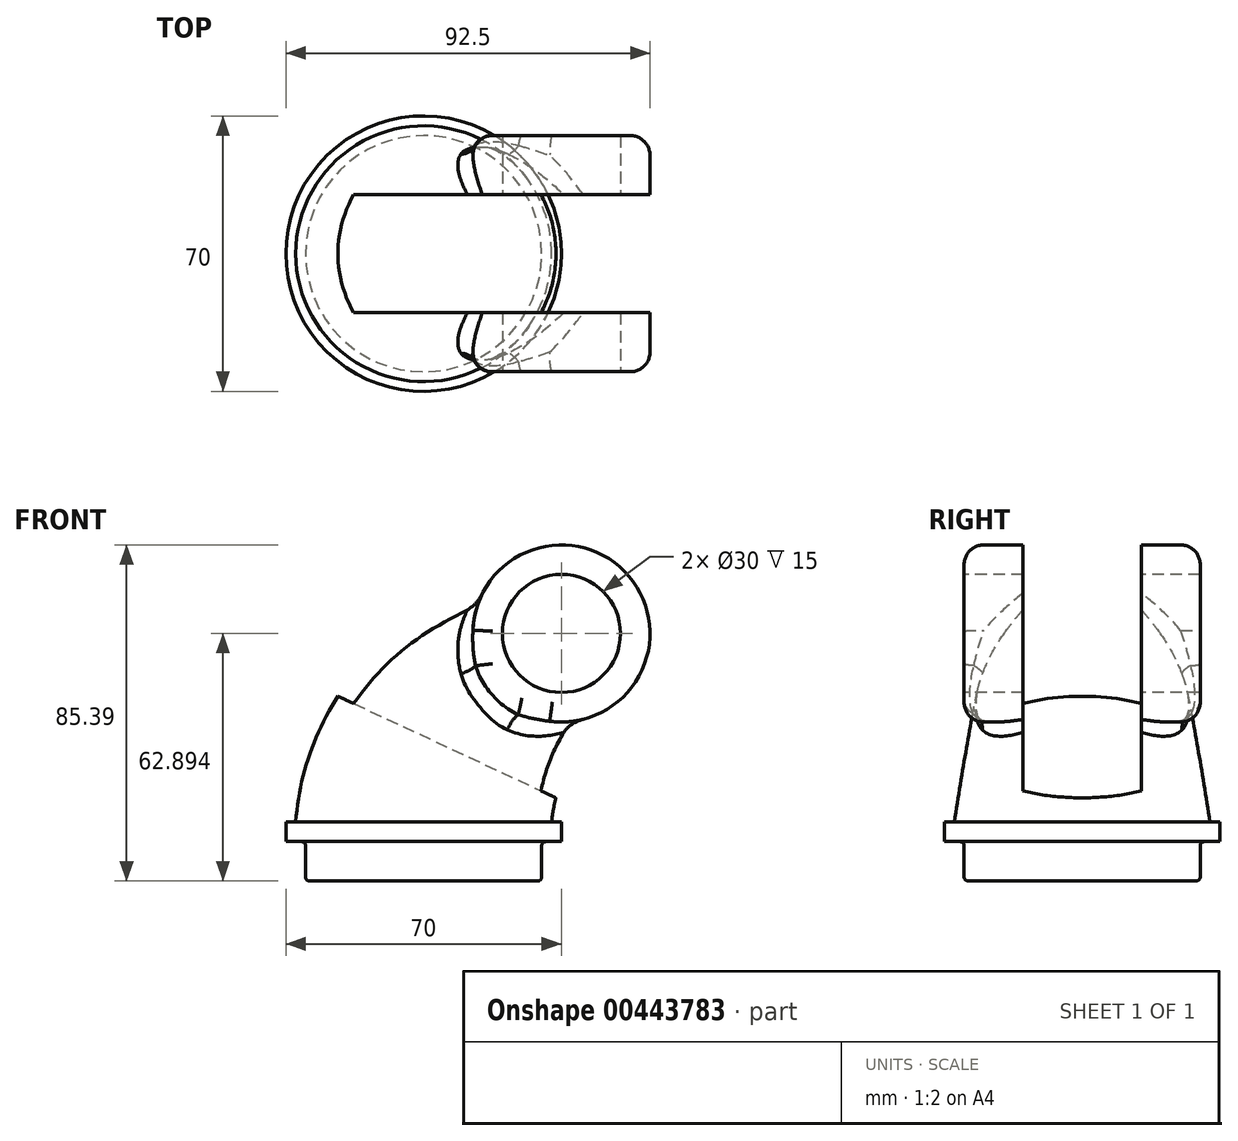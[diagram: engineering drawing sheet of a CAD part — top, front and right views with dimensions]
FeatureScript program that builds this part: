
annotation { "Feature Type Name" : "Feature", "Feature Type Description" : "" }
export const myFeature = defineFeature(function(context is Context, id is Id, definition is map)
    precondition{}
    {
        {
            var Q0;
            Q0=qCreatedBy(makeId("Top.planeOp"),FACE);
            var sketch = newSketch(context, id + "F0", { "sketchPlane" : qUnion([Q0])});
            skCircle(sketch, "E0", {"center": v(0, 0) * mm, "radius": 35 * mm});
            skSolve(sketch);
        }
        {
            var Q0;
            Q0 = qSketchRegion(id + "F0", true);
            extrude(context, id + "F1", {"entities" : qUnion([Q0]), "depth" : 5 * mm});
        }
        {
            var Q0;
            Q0=qCreatedBy(makeId("Front.planeOp"),FACE);
            var sketch = newSketch(context, id + "F2", { "sketchPlane" : qUnion([Q0])});
            skArc(sketch, "E1", {"start": v(17.6, 38.3) * mm, "mid": v(5.55, 23.37) * mm, "end": v(0, 5) * mm});
            skLineSegment(sketch, "E2", {"start": v(17.6, 38.3) * mm, "end": v(35, 52.9) * mm});
            skSolve(sketch);
        }
        {
            var Q0;
            Q0=sQuery(id+"F2.wireOp",EDGE,"E2");
            var Q1;
            Q1=sQuery(id+"F2.wireOp",VERTEX,"E2.end");
            cPlane(context, id + "F3", {"entities" : qUnion([Q0, Q1]), "cplaneType" : CPlaneType.LINE_POINT, "offset" : 25 * mm, "width" : 150 * mm, "height" : 150 * mm});
        }
        {
            var Q0;
            Q0=qCreatedBy(id+"F3.planeOp",FACE);
            var sketch = newSketch(context, id + "F4", { "sketchPlane" : qUnion([Q0])});
            skCircle(sketch, "E3", {"center": v(0, 18.02) * mm, "radius": 22.5 * mm});
            skSolve(sketch);
        }
        {
            var Q0;
            Q0=makeQuery(id+"F1.opExtrude","CAP_FACE",FACE,{"disambiguationData":[OSD([sQuery(id+"F0.wireOp",EDGE,"E0")])],"isStart":false});
            var sketch = newSketch(context, id + "F5", { "sketchPlane" : qUnion([Q0])});
            skCircle(sketch, "E4", {"center": v(0, 0) * mm, "radius": 32.5 * mm});
            skSolve(sketch);
        }
        {
            var Q0;
            Q0=qCreatedBy(makeId("Front.planeOp"),FACE);
            var sketch = newSketch(context, id + "F6", { "sketchPlane" : qUnion([Q0])});
            skArc(sketch, "E5", {"start": v(0.95, 58.66) * mm, "mid": v(-22.4, 35.96) * mm, "end": v(-32.5, 5) * mm});
            skLineSegment(sketch, "E6", {"start": v(0.95, 58.66) * mm, "end": v(20.54, 70.13) * mm});
            skSolve(sketch);
        }
        {
            var Q0;
            Q0=qCreatedBy(makeId("Front.planeOp"),FACE);
            var sketch = newSketch(context, id + "F7", { "sketchPlane" : qUnion([Q0])});
            skArc(sketch, "E7", {"start": v(48.46, 34.82) * mm, "mid": v(37.6, 21.45) * mm, "end": v(32.5, 5) * mm});
            skLineSegment(sketch, "E8", {"start": v(48.46, 34.82) * mm, "end": v(49.46, 35.66) * mm});
            skSolve(sketch);
        }
        {
            var Q1;
            Q1=makeQuery(id+"F5.imprint","IMPRINT",FACE,{"disambiguationData":[TD([[makeQuery(id+"F5.imprint","IMPRINT",EDGE,{"derivedFrom":sQuery(id+"F5.wireOp",EDGE,"E4")}),1.0]])]});
            var Q2;
            Q2=makeQuery(id+"F4.imprint","IMPRINT",FACE,{"disambiguationData":[TD([[makeQuery(id+"F4.imprint","IMPRINT",EDGE,{"derivedFrom":sQuery(id+"F4.wireOp",EDGE,"E3")}),1.0]])]});
            var Q3;
            Q3 = qConstructionFilter(qBodyType(qCreatedBy(id + "F7" ,EDGE), BodyType.WIRE), ConstructionObject.NO);
            var Q4;
            Q4 = qConstructionFilter(qBodyType(qCreatedBy(id + "F6" ,EDGE), BodyType.WIRE), ConstructionObject.NO);
            loft(context, id + "F8", {"operationType" : NewBodyOperationType.ADD, "addGuides" : true, "sheetProfilesArray" : [{ "sheetProfileEntities" : qUnion([Q1]) }, { "sheetProfileEntities" : qUnion([Q2]) }], "guidesArray" : [{ "guideEntities" : qUnion([Q3]), "guideDerivativeType" : LoftGuideDerivativeType.DEFAULT, "guideDerivativeMagnitude" : 1 }, { "guideEntities" : qUnion([Q4]), "guideDerivativeType" : LoftGuideDerivativeType.DEFAULT, "guideDerivativeMagnitude" : 1 }]});
        }
        {
            var Q0;
            Q0=qCreatedBy(makeId("Front.planeOp"),FACE);
            var sketch = newSketch(context, id + "F9", { "sketchPlane" : qUnion([Q0])});
            skCircle(sketch, "E9", {"center": v(35, 52.9) * mm, "radius": 22.5 * mm});
            skSolve(sketch);
        }
        {
            var Q0;
            Q0 = qSketchRegion(id + "F9", true);
            extrude(context, id + "F10", {"entities" : qUnion([Q0]), "operationType" : NewBodyOperationType.ADD, "endBound" : BoundingType.SYMMETRIC, "depth" : 60 * mm});
        }
        {
            var Q0;
            Q0=makeQuery(id+"F10.boolean.opBoolean","INTERSECT",EDGE,{"derivedFrom":[makeQuery(id+"F8.opLoft","SWEPT_FACE",FACE,{"disambiguationData":[OSD([sQuery(id+"F4.wireOp",EDGE,"E3"),sQuery(id+"F5.wireOp",EDGE,"E4"),sQuery(id+"F6.wireOp",VERTEX,"E6.start"),sQuery(id+"F6.wireOp",EDGE,"E5"),sQuery(id+"F6.wireOp",EDGE,"E6"),sQuery(id+"F7.wireOp",VERTEX,"E8.start"),sQuery(id+"F7.wireOp",EDGE,"E7"),sQuery(id+"F7.wireOp",EDGE,"E8")])]}),makeQuery(id+"F10.opExtrude","SWEPT_FACE",FACE,{"disambiguationData":[OSD([sQuery(id+"F9.wireOp",EDGE,"E9")])]})]});
            fillet(context, id + "F11", {"entities" : qUnion([Q0]), "radius" : 5 * mm, "tangentPropagation" : true, "allowEdgeOverflow" : false});
        }
        {
            var Q0;
            Q0=makeQuery(id+"F10.opExtrude","CAP_EDGE",EDGE,{"disambiguationData":[OSD([sQuery(id+"F9.wireOp",EDGE,"E9")])],"isStart":true});
            var Q1;
            Q1=makeQuery(id+"F10.opExtrude","CAP_EDGE",EDGE,{"disambiguationData":[OSD([sQuery(id+"F9.wireOp",EDGE,"E9")])],"isStart":false});
            fillet(context, id + "F12", {"entities" : qUnion([Q0, Q1]), "radius" : 5 * mm, "tangentPropagation" : true, "allowEdgeOverflow" : false});
        }
        {
            var Q0;
            Q0=makeQuery(id+"F10.opExtrude","CAP_FACE",FACE,{"disambiguationData":[OSD([sQuery(id+"F9.wireOp",EDGE,"E9")])],"isStart":false});
            var sketch = newSketch(context, id + "F13", { "sketchPlane" : qUnion([Q0])});
            skCircle(sketch, "E10", {"center": v(35, 52.9) * mm, "radius": 15 * mm});
            skSolve(sketch);
        }
        {
            var Q0;
            Q0 = qSketchRegion(id + "F13", true);
            extrude(context, id + "F14", {"entities" : qUnion([Q0]), "operationType" : NewBodyOperationType.REMOVE, "endBound" : BoundingType.THROUGH_ALL, "oppositeDirection" : true, "depth" : 25 * mm});
        }
        {
            var Q0;
            Q0=qCreatedBy(makeId("Front.planeOp"),FACE);
            var sketch = newSketch(context, id + "F15", { "sketchPlane" : qUnion([Q0])});
            skLineSegment(sketch, "E11", {"start": v(-100.76, 73.8) * mm, "end": v(57.5, 0) * mm});
            skLineSegment(sketch, "E12", {"start": v(57.5, 75.66) * mm, "end": v(57.5, 0) * mm});
            skLineSegment(sketch, "E13", {"start": v(-100.76, 73.8) * mm, "end": v(57.5, 75.66) * mm});
            skSolve(sketch);
        }
        {
            var Q0;
            Q0 = qSketchRegion(id + "F15", true);
            extrude(context, id + "F16", {"entities" : qUnion([Q0]), "operationType" : NewBodyOperationType.REMOVE, "endBound" : BoundingType.SYMMETRIC, "oppositeDirection" : true, "depth" : 30 * mm});
        }
        {
            var Q0;
            Q0=qCreatedBy(makeId("Front.planeOp"),FACE);
            var sketch = newSketch(context, id + "F17", { "sketchPlane" : qUnion([Q0])});
            skLineSegment(sketch, "E14.bottom", {"start": v(0, 0) * mm, "end": v(-30, 0) * mm});
            skLineSegment(sketch, "E14.top", {"start": v(0, -10) * mm, "end": v(-30, -10) * mm});
            skLineSegment(sketch, "E14.left", {"start": v(0, 0) * mm, "end": v(0, -10) * mm});
            skLineSegment(sketch, "E14.right", {"start": v(-30, 0) * mm, "end": v(-30, -10) * mm});
            skSolve(sketch);
        }
        {
            var Q0;
            Q0 = qSketchRegion(id + "F17", true);
            var Q1;
            Q1=sQuery(id+"F17.wireOp",EDGE,"E14.left");
            revolve(context, id + "F18", {"operationType" : NewBodyOperationType.ADD, "entities" : qUnion([Q0]), "axis" : qUnion([Q1]), "revolveType" : RevolveType.FULL});
        }
        {
            var Q0;
            Q0=makeQuery(id+"F18.opRevolve","SWEPT_FACE",FACE,{"disambiguationData":[OSD([sQuery(id+"F17.wireOp",EDGE,"E14.right")])]});
            fillet(context, id + "F19", {"entities" : qUnion([Q0]), "radius" : 1 * mm, "tangentPropagation" : true, "allowEdgeOverflow" : false});
        }
    });
